# Revit family: Loaded-Windows_Roof-Windows_FAKRO_Access-roof-light-DRL_IFC-USA-27½x59½
name_source: partatom
category: Okna
revit_build: Autodesk Revit 2015 (Build: 20140606_1530(x64)
units: mm (PartAtom-declared; Revit-internal decimal feet)

## types (1)
- DRL 27½ x 59½
    Air permeability = Class 4
    BIMobject category = Construction - Access doors & panels
    Brand url = http://www.fakro.com
    CSI MasterFormat 2016 Code = 07 72 33
    CSI MasterFormat 2016 Title = Roof Hatches
    Colour = White RAL 9003
    Design country = Poland
    Edition number = 1
    External fire performance = Npd
    Glass perimeter ["] = 187"
    Handle Material = Aluminium - FAKRO - RAL9003 - Handle
    Harmonised technical specification = EN 14351-1:2006+A1:2010
    Impact resistance = Class 5 - 950mm
    Installation instructions DRL = https://www.fakrousa.com
    Kod zespołu = B3020110
    Load-bearing capacity of safety device = Threshold value
    Manufacturer country = Poland
    Manufacturer name = FAKRO
    Material = Frame PVC
    Material Actuators = Aluminium - FAKRO - RAL9006 - Actuators
    Material External = Aluminium - FAKRO - RAL7022 - Flashing
    Material Internal = Plastic - FAKRO - RAL9003 - Frame PVC
    Material main = Steel
    Material secondary = PVC
    Max window opening angle = 60.00°
    Model = DRL
    Nominal height = 8"
    Nominal length = 68 7/8"
    Nominal width = 35 3/8"
    Obj Type = 4
    OmniClass Code = 21-02 03 06 05
    OmniClass Description = Vents and Hatches
    Opening method = Top hung
    Operation mode = Manual
    Opis = Flat roof metal hatch
    Producent = FAKRO
    Product family = Roof Hatches
    Product group = Roof Hatches
    Product url = https://www.fakrousa.com
    Reaction to fire = Npd
    Resistance to snow load = Npd
    Resistance to wind load = Class C5/B5
    Roof angle = 0-5°
    Seal Material = Rubber - FAKRO - RAL9005 - Seal
    Technical description = https://www.fakrousa.com
    Thermal insulation of frame and glazing connection (psi) [BTU/h ftF] = Npd
    UNSPSC Category = Roofing accessories
    UNSPSC Code = 301516
    URL = www.fakrousa.com
    Uniformat II Code = B3060,50
    Uniformat II Description = Vents and Hatches
    Warning = The present model is for informational-demonstrative purposes only and as such cannot constitute a basis for performance. All dimensions presented in this model should be verified on site. Because of the fact that the model is a schematic one, FAKRO shall not assume any responsibility for the actual installation quality on the roof.
    Watertightness / unshielded (A) = E900
    Weight Net (Kg) = 69
    Weight Net (lbs) = 152
    Window acoustic performance Rw [dB] = 30(0;-2)
    Window perimeter ["] = 208 5/8"
    Youtube clip = https://www.fakrousa.com
